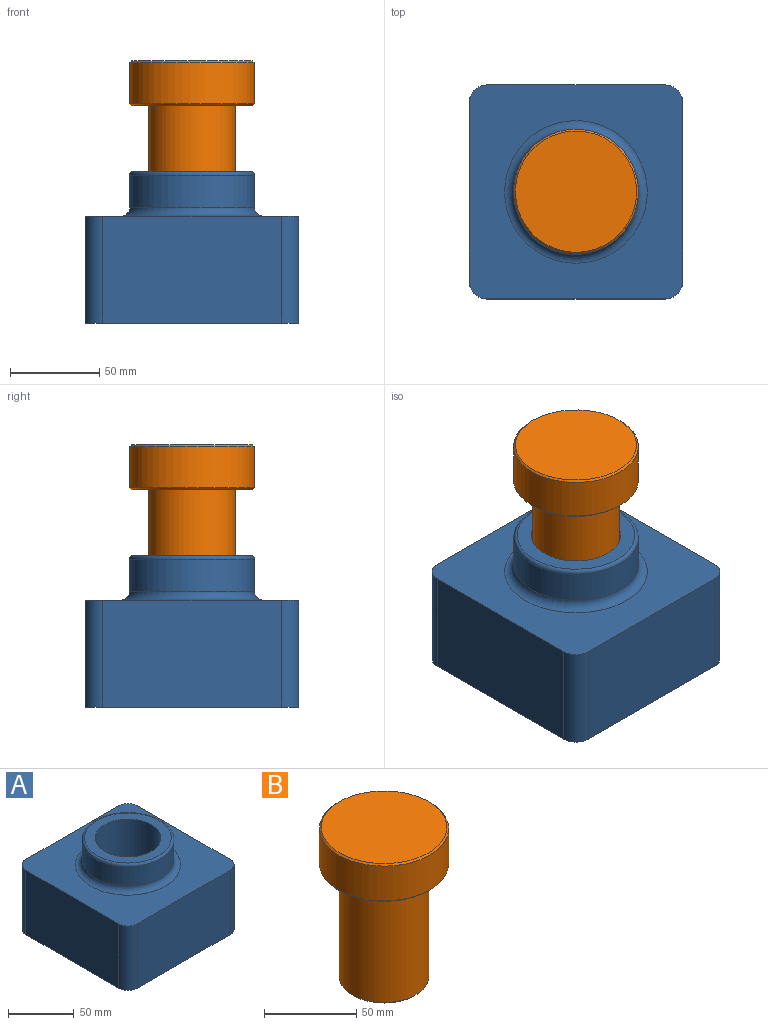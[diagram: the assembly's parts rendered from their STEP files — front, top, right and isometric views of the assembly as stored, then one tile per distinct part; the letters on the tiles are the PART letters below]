
ASSEMBLY  parts=2 mates=2
PART A: 29 faces, bbox 120x120x85 mm
  f0: plane 120x120mm, normal (0,0,-1), area 913.1mm2, adj f1,f2,f3,f4,f12,f13,f14,f15
  f1: plane 100x60mm, normal (1,0,0), area 6000mm2, adj f0,f5,f12,f15
  f2: plane 100x60mm, normal (0,1,0), area 6000mm2, adj f0,f5,f12,f13
  f3: plane 100x60mm, normal (-1,0,0), area 6000mm2, adj f0,f5,f13,f14
  f4: plane 100x60mm, normal (0,-1,0), area 6000mm2, adj f0,f5,f14,f15
  f5: plane 120x120mm, normal (0,0,1), area 9287.6mm2, adj f1,f2,f3,f4,f10,f12,f13,f14
  f6: plane 54x54mm, normal (0,0,-1), area 326.7mm2, adj f9,f23
  f7: cylinder r=35mm len=70mm, axis (0,0,-1), area 3958.4mm2, adj f10,f11
  f8: plane 66x66mm, normal (0,0,1), area 1457.7mm2, adj f9,f11
  f9: cylinder r=25mm len=85mm, axis (0,0,1), area 13351.8mm2, adj f6,f8
  f10: torus R=40mm, axis (0,0,1), area 1816.8mm2, adj f5,f7
  f11: torus R=33mm, axis (0,0,1), area 676.5mm2, adj f7,f8
  f12: cylinder r=10mm len=60mm, axis (0,0,1), area 942.5mm2, adj f0,f1,f2,f5
  f13: cylinder r=10mm len=60mm, axis (0,0,-1), area 942.5mm2, adj f0,f2,f3,f5
  f14: cylinder r=10mm len=60mm, axis (0,0,1), area 942.5mm2, adj f0,f3,f4,f5
  f15: cylinder r=10mm len=60mm, axis (0,0,-1), area 942.5mm2, adj f0,f1,f4,f5
  f16: plane 100x58mm, normal (-1,0,0), area 5800mm2, adj f0,f20,f25,f28
  f17: plane 100x58mm, normal (0,-1,0), area 5800mm2, adj f0,f20,f25,f26
  f18: plane 100x58mm, normal (1,0,0), area 5800mm2, adj f0,f20,f26,f27
  f19: plane 100x58mm, normal (0,1,0), area 5800mm2, adj f0,f20,f27,f28
  f20: plane 116x116mm, normal (0,0,-1), area 8374.5mm2, adj f16,f17,f18,f19,f24,f25,f26,f27
  f21: cylinder r=33mm len=66mm, axis (0,0,-1), area 3732.2mm2, adj f22,f24
  f22: plane 66x66mm, normal (0,0,-1), area 1131mm2, adj f21,f23
  f23: cylinder r=27mm len=83mm, axis (0,0,1), area 14080.6mm2, adj f6,f22
  f24: torus R=40mm, axis (0,0,1), area 2455.6mm2, adj f20,f21
  f25: cylinder r=8mm len=58mm, axis (0,0,1), area 728.8mm2, adj f0,f16,f17,f20
  f26: cylinder r=8mm len=58mm, axis (0,0,-1), area 728.8mm2, adj f0,f17,f18,f20
  f27: cylinder r=8mm len=58mm, axis (0,0,1), area 728.8mm2, adj f0,f18,f19,f20
  f28: cylinder r=8mm len=58mm, axis (0,0,-1), area 728.8mm2, adj f0,f16,f19,f20
PART B: 8 faces, bbox 70x70x100 mm
  f0: plane 46.5x46.5mm, normal (0,0,-1), area 1698.2mm2, adj f5
  f1: cylinder r=24.25mm len=74mm, axis (0,0,1), area 11275.2mm2, adj f2,f5
  f2: plane 68x68mm, normal (0,0,-1), area 1784.2mm2, adj f1,f6
  f3: cylinder r=35mm len=70mm, axis (0,0,1), area 5058mm2, adj f6,f7
  f4: plane 68x68mm, normal (0,0,1), area 3631.7mm2, adj f7
  f5: cone r=24.25mm half-angle=45deg, axis (0,0,1), area 211mm2, adj f0,f1
  f6: cone r=35mm half-angle=45deg, axis (0,0,1), area 306.6mm2, adj f2,f3
  f7: cone r=34mm half-angle=45deg, axis (0,0,-1), area 306.6mm2, adj f3,f4
PLACE A t=(-7.78,49.89,21.99)mm
PLACE B t=(-7.78,49.89,68.99)mm
MATE revolute B.f1 <-> A.f9  axis (0,0,1) through (-7.78,49.89,106.99)mm
MATE slider B.f1 <-> A.f7  axis (0,0,-1) through (-7.78,49.89,143.99)mm
